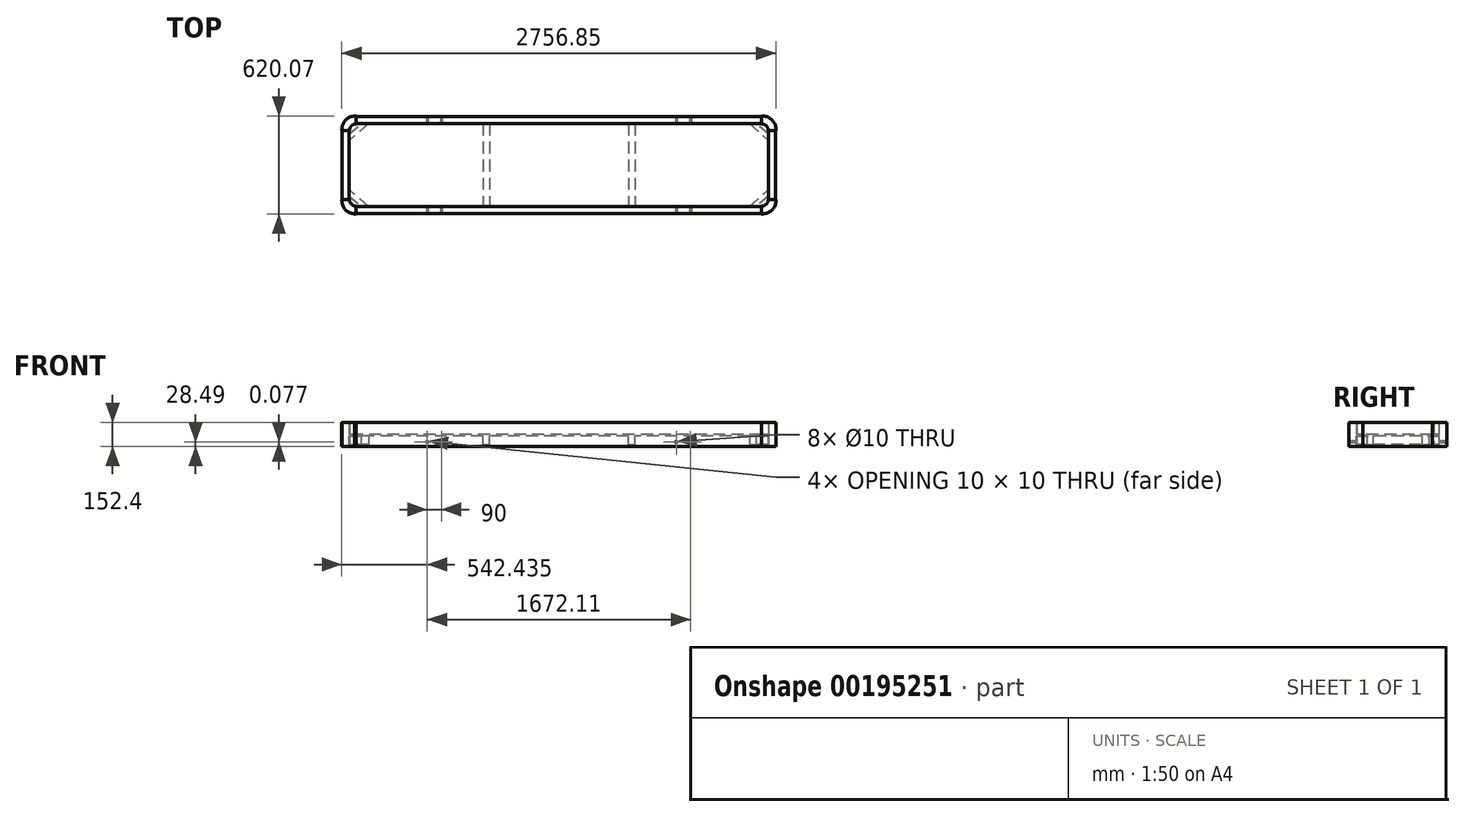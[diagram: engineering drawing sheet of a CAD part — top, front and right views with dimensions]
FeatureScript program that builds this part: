
annotation { "Feature Type Name" : "Feature", "Feature Type Description" : "" }
export const myFeature = defineFeature(function(context is Context, id is Id, definition is map)
    precondition{}
    {
        {
            var Q0;
            Q0=qCreatedBy(makeId("Top.planeOp"),FACE);
            var sketch = newSketch(context, id + "F0", { "sketchPlane" : qUnion([Q0])});
            skLineSegment(sketch, "E0.bottom", {"start": v(-1376.36, -307.98) * mm, "end": v(1376.36, -307.98) * mm});
            skLineSegment(sketch, "E0.top", {"start": v(-1376.36, 307.98) * mm, "end": v(1376.36, 307.98) * mm});
            skLineSegment(sketch, "E0.left", {"start": v(-1376.36, -307.98) * mm, "end": v(-1376.36, 307.98) * mm});
            skLineSegment(sketch, "E0.right", {"start": v(1376.36, -307.98) * mm, "end": v(1376.36, 307.98) * mm});
            skPoint(sketch, "E0.middle", {"position": v(0, 0) * mm});
            skSolve(sketch);
        }
        {
            var Q0;
            Q0=makeQuery(id+"F0.imprint","IMPRINT",FACE,{"disambiguationData":[TD([[makeQuery(id+"F0.imprint","IMPRINT",EDGE,{"derivedFrom":sQuery(id+"F0.wireOp",EDGE,"E0.bottom")}),1.0]])]});
            var Q1;
            Q1 = qSketchRegion(id + "F3", true);
            extrude(context, id + "F1", {"entities" : qUnion([Q0, Q1]), "oppositeDirection" : true, "depth" : 10.16 * mm});
        }
        {
            var Q0;
            Q0=makeQuery(id+"F1.opExtrude","SWEPT_EDGE",EDGE,{"disambiguationData":[OSD([sQuery(id+"F0.wireOp",EDGE,"E0.top"),sQuery(id+"F0.wireOp",EDGE,"E0.right")])]});
            var Q1;
            Q1=makeQuery(id+"F1.opExtrude","SWEPT_EDGE",EDGE,{"disambiguationData":[OSD([sQuery(id+"F0.wireOp",EDGE,"E0.bottom"),sQuery(id+"F0.wireOp",EDGE,"E0.right")])]});
            var Q2;
            Q2=makeQuery(id+"F1.opExtrude","SWEPT_EDGE",EDGE,{"disambiguationData":[OSD([sQuery(id+"F0.wireOp",EDGE,"E0.bottom"),sQuery(id+"F0.wireOp",EDGE,"E0.left")])]});
            var Q3;
            Q3=makeQuery(id+"F1.opExtrude","SWEPT_EDGE",EDGE,{"disambiguationData":[OSD([sQuery(id+"F0.wireOp",EDGE,"E0.top"),sQuery(id+"F0.wireOp",EDGE,"E0.left")])]});
            fillet(context, id + "F2", {"entities" : qUnion([Q0, Q1, Q2, Q3]), "radius" : 80 * mm, "allowEdgeOverflow" : false});
        }
        {
            var Q0;
            Q0=qCreatedBy(makeId("Top.planeOp"),FACE);
            var sketch = newSketch(context, id + "F3", { "sketchPlane" : qUnion([Q0])});
            skArc(sketch, "E1.0", {"start": v(-1296.36, 307.98) * mm, "mid": v(-1352.93, 284.54) * mm, "end": v(-1376.36, 227.98) * mm});
            skLineSegment(sketch, "E1.1", {"start": v(-1376.36, -227.98) * mm, "end": v(-1376.36, 227.98) * mm});
            skLineSegment(sketch, "E1.2", {"start": v(-1296.36, 307.98) * mm, "end": v(1296.36, 307.98) * mm});
            skArc(sketch, "E1.3", {"start": v(-1376.36, -227.98) * mm, "mid": v(-1352.93, -284.54) * mm, "end": v(-1296.36, -307.98) * mm});
            skArc(sketch, "E1.4", {"start": v(1376.36, 227.98) * mm, "mid": v(1352.93, 284.54) * mm, "end": v(1296.36, 307.98) * mm});
            skLineSegment(sketch, "E1.5", {"start": v(1376.36, -227.98) * mm, "end": v(1376.36, 227.98) * mm});
            skArc(sketch, "E1.6", {"start": v(1296.36, -307.98) * mm, "mid": v(1352.93, -284.54) * mm, "end": v(1376.36, -227.98) * mm});
            skLineSegment(sketch, "E1.7", {"start": v(-1296.36, -307.98) * mm, "end": v(1296.36, -307.98) * mm});
            skArc(sketch, "E2.0", {"start": v(-1331.91, -262.98) * mm, "mid": v(-1331.75, -263.36) * mm, "end": v(-1331.36, -263.53) * mm});
            skArc(sketch, "E2.3", {"start": v(-1331.36, 263.53) * mm, "mid": v(-1331.75, 263.36) * mm, "end": v(-1331.91, 262.98) * mm});
            skArc(sketch, "E2.4", {"start": v(1331.36, -263.53) * mm, "mid": v(1331.75, -263.36) * mm, "end": v(1331.91, -262.98) * mm});
            skArc(sketch, "E2.6", {"start": v(1331.91, 262.98) * mm, "mid": v(1331.75, 263.36) * mm, "end": v(1331.36, 263.53) * mm});
            skArc(sketch, "E3.0", {"start": v(-1286.91, 263.53) * mm, "mid": v(-1318.73, 250.34) * mm, "end": v(-1331.91, 218.53) * mm});
            skLineSegment(sketch, "E3.2", {"start": v(-1286.91, 263.53) * mm, "end": v(1286.91, 263.53) * mm});
            skArc(sketch, "E3.4", {"start": v(1331.91, 220.25) * mm, "mid": v(1318.13, 250.95) * mm, "end": v(1286.91, 263.53) * mm});
            skArc(sketch, "E4.MirrorCS", {"start": v(-1286.91, -263.53) * mm, "mid": v(-1318.73, -250.34) * mm, "end": v(-1331.91, -218.53) * mm});
            skLineSegment(sketch, "E5.MirrorCS", {"start": v(-1286.91, -263.53) * mm, "end": v(1286.91, -263.53) * mm});
            skArc(sketch, "E6.MirrorCS", {"start": v(1331.91, -220.25) * mm, "mid": v(1318.13, -250.95) * mm, "end": v(1286.91, -263.53) * mm});
            skLineSegment(sketch, "E7", {"start": v(-1331.91, -218.53) * mm, "end": v(-1331.91, 218.53) * mm});
            skLineSegment(sketch, "E8", {"start": v(1331.91, -220.25) * mm, "end": v(1331.91, 220.25) * mm});
            skSolve(sketch);
        }
        {
            var Q0;
            Q0 = qSketchRegion(id + "F3", true);
            extrude(context, id + "F4", {"entities" : qUnion([Q0]), "operationType" : NewBodyOperationType.ADD, "endBound" : BoundingType.SYMMETRIC, "depth" : 149.86 * mm});
        }
        {
            var Q0;
            Q0=qCreatedBy(makeId("Top.planeOp"),FACE);
            var sketch = newSketch(context, id + "F5", { "sketchPlane" : qUnion([Q0])});
            skArc(sketch, "E9.0", {"start": v(-1378.36, -227.98) * mm, "mid": v(-1354.35, -285.96) * mm, "end": v(-1296.36, -309.98) * mm});
            skArc(sketch, "E10.0", {"start": v(-1296.36, 309.98) * mm, "mid": v(-1354.35, 285.96) * mm, "end": v(-1378.36, 227.98) * mm});
            skArc(sketch, "E11.0", {"start": v(1296.36, -309.98) * mm, "mid": v(1354.35, -285.96) * mm, "end": v(1378.36, -227.98) * mm});
            skArc(sketch, "E12.0", {"start": v(1378.36, 227.98) * mm, "mid": v(1354.35, 285.96) * mm, "end": v(1296.36, 309.98) * mm});
            skArc(sketch, "E13.0", {"start": v(1329.93, 219.82) * mm, "mid": v(1316.4, 249.84) * mm, "end": v(1285.61, 261.5) * mm});
            skArc(sketch, "E14.0", {"start": v(1329.9, -220.42) * mm, "mid": v(1316.53, -249.71) * mm, "end": v(1286.57, -261.52) * mm});
            skArc(sketch, "E15.0", {"start": v(-1286.91, -261.53) * mm, "mid": v(-1317.32, -248.93) * mm, "end": v(-1329.91, -218.53) * mm});
            skArc(sketch, "E16.0", {"start": v(-1286.9, 261.52) * mm, "mid": v(-1317.32, 248.93) * mm, "end": v(-1329.91, 218.53) * mm});
            skLineSegment(sketch, "E17", {"start": v(-1286.9, 261.52) * mm, "end": v(-1286.9, 309.98) * mm});
            skLineSegment(sketch, "E18", {"start": v(-1286.9, 309.98) * mm, "end": v(-1296.36, 309.98) * mm});
            skLineSegment(sketch, "E19", {"start": v(-1329.91, 218.53) * mm, "end": v(-1378.49, 218.53) * mm});
            skLineSegment(sketch, "E20", {"start": v(-1378.49, 218.53) * mm, "end": v(-1378.36, 227.98) * mm});
            skLineSegment(sketch, "E21", {"start": v(1285.61, 261.5) * mm, "end": v(1285.61, 309.98) * mm});
            skLineSegment(sketch, "E22", {"start": v(1285.61, 309.98) * mm, "end": v(1296.36, 309.98) * mm});
            skLineSegment(sketch, "E23", {"start": v(1329.93, 219.82) * mm, "end": v(1378.36, 219.82) * mm});
            skLineSegment(sketch, "E24", {"start": v(1378.36, 219.82) * mm, "end": v(1378.36, 227.98) * mm});
            skLineSegment(sketch, "E25", {"start": v(1286.57, -261.52) * mm, "end": v(1286.57, -309.98) * mm});
            skLineSegment(sketch, "E26", {"start": v(1286.57, -309.98) * mm, "end": v(1296.36, -309.98) * mm});
            skLineSegment(sketch, "E27", {"start": v(1329.9, -220.42) * mm, "end": v(1378.36, -220.42) * mm});
            skLineSegment(sketch, "E28", {"start": v(1378.36, -220.42) * mm, "end": v(1378.36, -227.98) * mm});
            skLineSegment(sketch, "E29", {"start": v(-1329.91, -218.53) * mm, "end": v(-1378.45, -218.53) * mm});
            skLineSegment(sketch, "E30", {"start": v(-1378.45, -218.53) * mm, "end": v(-1378.36, -227.98) * mm});
            skLineSegment(sketch, "E31", {"start": v(-1286.91, -261.53) * mm, "end": v(-1286.91, -310.09) * mm});
            skLineSegment(sketch, "E32", {"start": v(-1286.91, -310.09) * mm, "end": v(-1296.36, -309.98) * mm});
            skSolve(sketch);
        }
        {
            var Q0;
            Q0 = qSketchRegion(id + "F5", true);
            extrude(context, id + "F6", {"entities" : qUnion([Q0]), "operationType" : NewBodyOperationType.ADD, "endBound" : BoundingType.SYMMETRIC, "depth" : 152.4 * mm});
        }
        {
            var Q0;
            Q0=makeQuery(id+"F4.opExtrude","CAP_EDGE",EDGE,{"disambiguationData":[OSD([sQuery(id+"F3.wireOp",EDGE,"E2.5")])],"isStart":false});
            var Q1;
            Q1=makeQuery(id+"F4.opExtrude","CAP_EDGE",EDGE,{"disambiguationData":[OSD([sQuery(id+"F3.wireOp",EDGE,"E1.5")])],"isStart":false});
            var Q2;
            Q2=makeQuery(id+"F4.opExtrude","CAP_EDGE",EDGE,{"disambiguationData":[OSD([sQuery(id+"F3.wireOp",EDGE,"E1.1")])],"isStart":false});
            var Q3;
            Q3=makeQuery(id+"F4.opExtrude","CAP_EDGE",EDGE,{"disambiguationData":[OSD([sQuery(id+"F3.wireOp",EDGE,"E2.1")])],"isStart":false});
            var Q4;
            Q4=makeQuery(id+"F4.opExtrude","CAP_EDGE",EDGE,{"disambiguationData":[OSD([sQuery(id+"F3.wireOp",EDGE,"E2.2")])],"isStart":false});
            var Q5;
            Q5=makeQuery(id+"F4.opExtrude","CAP_EDGE",EDGE,{"disambiguationData":[OSD([sQuery(id+"F3.wireOp",EDGE,"E1.7")])],"isStart":false});
            var Q6;
            Q6=makeQuery(id+"F4.opExtrude","CAP_EDGE",EDGE,{"disambiguationData":[OSD([sQuery(id+"F3.wireOp",EDGE,"E1.2")])],"isStart":false});
            var Q7;
            Q7=makeQuery(id+"F4.opExtrude","CAP_EDGE",EDGE,{"disambiguationData":[OSD([sQuery(id+"F3.wireOp",EDGE,"E2.7")])],"isStart":false});
            fillet(context, id + "F7", {"entities" : qUnion([Q0, Q1, Q2, Q3, Q4, Q5, Q6, Q7]), "radius" : .4 * mm, "tangentPropagation" : true, "allowEdgeOverflow" : false});
        }
        {
            var Q0;
            Q0=makeQuery(id+"F6.opExtrude","CAP_EDGE",EDGE,{"disambiguationData":[OSD([sQuery(id+"F5.wireOp",EDGE,"E9.0")])],"isStart":true});
            var Q1;
            Q1=makeQuery(id+"F6.opExtrude","CAP_EDGE",EDGE,{"disambiguationData":[OSD([sQuery(id+"F5.wireOp",EDGE,"E30")])],"isStart":true});
            var Q2;
            Q2=makeQuery(id+"F6.opExtrude","CAP_EDGE",EDGE,{"disambiguationData":[OSD([sQuery(id+"F5.wireOp",EDGE,"E32")])],"isStart":true});
            var Q3;
            Q3=makeQuery(id+"F6.opExtrude","CAP_EDGE",EDGE,{"disambiguationData":[OSD([sQuery(id+"F5.wireOp",EDGE,"E15.0")])],"isStart":true});
            var Q4;
            Q4=makeQuery(id+"F6.opExtrude","CAP_EDGE",EDGE,{"disambiguationData":[OSD([sQuery(id+"F5.wireOp",EDGE,"E20")])],"isStart":true});
            var Q5;
            Q5=makeQuery(id+"F6.opExtrude","CAP_EDGE",EDGE,{"disambiguationData":[OSD([sQuery(id+"F5.wireOp",EDGE,"E10.0")])],"isStart":true});
            var Q6;
            Q6=makeQuery(id+"F6.opExtrude","CAP_EDGE",EDGE,{"disambiguationData":[OSD([sQuery(id+"F5.wireOp",EDGE,"E18")])],"isStart":true});
            var Q7;
            Q7=makeQuery(id+"F6.opExtrude","CAP_EDGE",EDGE,{"disambiguationData":[OSD([sQuery(id+"F5.wireOp",EDGE,"E16.0")])],"isStart":true});
            var Q8;
            Q8=makeQuery(id+"F6.opExtrude","CAP_EDGE",EDGE,{"disambiguationData":[OSD([sQuery(id+"F5.wireOp",EDGE,"E11.0")])],"isStart":true});
            var Q9;
            Q9=makeQuery(id+"F6.opExtrude","CAP_EDGE",EDGE,{"disambiguationData":[OSD([sQuery(id+"F5.wireOp",EDGE,"E14.0")])],"isStart":true});
            var Q10;
            Q10=makeQuery(id+"F6.opExtrude","CAP_EDGE",EDGE,{"disambiguationData":[OSD([sQuery(id+"F5.wireOp",EDGE,"E26")])],"isStart":true});
            var Q11;
            Q11=makeQuery(id+"F6.opExtrude","CAP_EDGE",EDGE,{"disambiguationData":[OSD([sQuery(id+"F5.wireOp",EDGE,"E28")])],"isStart":true});
            var Q12;
            Q12=makeQuery(id+"F6.opExtrude","CAP_EDGE",EDGE,{"disambiguationData":[OSD([sQuery(id+"F5.wireOp",EDGE,"E13.0")])],"isStart":true});
            var Q13;
            Q13=makeQuery(id+"F6.opExtrude","CAP_EDGE",EDGE,{"disambiguationData":[OSD([sQuery(id+"F5.wireOp",EDGE,"E24")])],"isStart":true});
            var Q14;
            Q14=makeQuery(id+"F6.opExtrude","CAP_EDGE",EDGE,{"disambiguationData":[OSD([sQuery(id+"F5.wireOp",EDGE,"E22")])],"isStart":true});
            var Q15;
            Q15=makeQuery(id+"F6.opExtrude","CAP_EDGE",EDGE,{"disambiguationData":[OSD([sQuery(id+"F5.wireOp",EDGE,"E12.0")])],"isStart":true});
            var Q16;
            Q16=makeQuery(id+"F6.opExtrude","SWEPT_EDGE",EDGE,{"disambiguationData":[OSD([sQuery(id+"F5.wireOp",EDGE,"E25"),sQuery(id+"F5.wireOp",EDGE,"E26")])]});
            var Q17;
            Q17=makeQuery(id+"F6.opExtrude","CAP_EDGE",EDGE,{"disambiguationData":[OSD([sQuery(id+"F5.wireOp",EDGE,"E15.0")])],"isStart":false});
            var Q18;
            Q18=makeQuery(id+"F6.opExtrude","CAP_EDGE",EDGE,{"disambiguationData":[OSD([sQuery(id+"F5.wireOp",EDGE,"E30")])],"isStart":false});
            var Q19;
            Q19=makeQuery(id+"F6.opExtrude","CAP_EDGE",EDGE,{"disambiguationData":[OSD([sQuery(id+"F5.wireOp",EDGE,"E9.0")])],"isStart":false});
            var Q20;
            Q20=makeQuery(id+"F6.opExtrude","CAP_EDGE",EDGE,{"disambiguationData":[OSD([sQuery(id+"F5.wireOp",EDGE,"E32")])],"isStart":false});
            var Q21;
            Q21=makeQuery(id+"F6.opExtrude","CAP_EDGE",EDGE,{"disambiguationData":[OSD([sQuery(id+"F5.wireOp",EDGE,"E16.0")])],"isStart":false});
            var Q22;
            Q22=makeQuery(id+"F6.opExtrude","CAP_EDGE",EDGE,{"disambiguationData":[OSD([sQuery(id+"F5.wireOp",EDGE,"E18")])],"isStart":false});
            var Q23;
            Q23=makeQuery(id+"F6.opExtrude","CAP_EDGE",EDGE,{"disambiguationData":[OSD([sQuery(id+"F5.wireOp",EDGE,"E10.0")])],"isStart":false});
            var Q24;
            Q24=makeQuery(id+"F6.opExtrude","CAP_EDGE",EDGE,{"disambiguationData":[OSD([sQuery(id+"F5.wireOp",EDGE,"E20")])],"isStart":false});
            var Q25;
            Q25=makeQuery(id+"F6.opExtrude","CAP_EDGE",EDGE,{"disambiguationData":[OSD([sQuery(id+"F5.wireOp",EDGE,"E14.0")])],"isStart":false});
            var Q26;
            Q26=makeQuery(id+"F6.opExtrude","CAP_EDGE",EDGE,{"disambiguationData":[OSD([sQuery(id+"F5.wireOp",EDGE,"E28")])],"isStart":false});
            var Q27;
            Q27=makeQuery(id+"F6.opExtrude","CAP_EDGE",EDGE,{"disambiguationData":[OSD([sQuery(id+"F5.wireOp",EDGE,"E11.0")])],"isStart":false});
            var Q28;
            Q28=makeQuery(id+"F6.opExtrude","CAP_EDGE",EDGE,{"disambiguationData":[OSD([sQuery(id+"F5.wireOp",EDGE,"E26")])],"isStart":false});
            var Q29;
            Q29=makeQuery(id+"F6.opExtrude","CAP_EDGE",EDGE,{"disambiguationData":[OSD([sQuery(id+"F5.wireOp",EDGE,"E12.0")])],"isStart":false});
            var Q30;
            Q30=makeQuery(id+"F6.opExtrude","CAP_EDGE",EDGE,{"disambiguationData":[OSD([sQuery(id+"F5.wireOp",EDGE,"E22")])],"isStart":false});
            var Q31;
            Q31=makeQuery(id+"F6.opExtrude","CAP_EDGE",EDGE,{"disambiguationData":[OSD([sQuery(id+"F5.wireOp",EDGE,"E13.0")])],"isStart":false});
            var Q32;
            Q32=makeQuery(id+"F6.opExtrude","CAP_EDGE",EDGE,{"disambiguationData":[OSD([sQuery(id+"F5.wireOp",EDGE,"E24")])],"isStart":false});
            fillet(context, id + "F8", {"entities" : qUnion([Q0, Q1, Q2, Q3, Q4, Q5, Q6, Q7, Q8, Q9, Q10, Q11, Q12, Q13, Q14, Q15, Q16, Q17, Q18, Q19, Q20, Q21, Q22, Q23, Q24, Q25, Q26, Q27, Q28, Q29, Q30, Q31, Q32]), "radius" : 1 * mm, "tangentPropagation" : true, "allowEdgeOverflow" : false});
        }
        {
            var Q0;
            Q0=qCreatedBy(makeId("Top.planeOp"),FACE);
            var sketch = newSketch(context, id + "F9", { "sketchPlane" : qUnion([Q0])});
            skLineSegment(sketch, "E33.bottom", {"start": v(-1359.8, 171.57) * mm, "end": v(-1220.1, 171.57) * mm, "construction": true});
            skLineSegment(sketch, "E33.left", {"start": v(-1330.9, 167.86) * mm, "end": v(-1330.9, 307.56) * mm, "construction": true});
            skLineSegment(sketch, "E34", {"start": v(-1359.8, 171.57) * mm, "end": v(-1233.38, 281.66) * mm});
            skLineSegment(sketch, "E35", {"start": v(-1189.58, 281.66) * mm, "end": v(-1233.38, 281.66) * mm});
            skLineSegment(sketch, "E36", {"start": v(-1189.58, 281.66) * mm, "end": v(-1342.65, 147.07) * mm});
            skLineSegment(sketch, "E37", {"start": v(-1359.8, 171.57) * mm, "end": v(-1342.65, 147.07) * mm});
            skLineSegment(sketch, "E38.MirrorCS", {"start": v(1359.8, 171.57) * mm, "end": v(1342.65, 147.07) * mm});
            skLineSegment(sketch, "E39.MirrorCS", {"start": v(1359.8, 171.57) * mm, "end": v(1233.38, 281.66) * mm});
            skLineSegment(sketch, "E40.MirrorCS", {"start": v(1189.58, 281.66) * mm, "end": v(1233.38, 281.66) * mm});
            skLineSegment(sketch, "E41.MirrorCS", {"start": v(1359.8, 171.57) * mm, "end": v(1220.1, 171.57) * mm, "construction": true});
            skLineSegment(sketch, "E42.MirrorCS", {"start": v(1330.9, 167.86) * mm, "end": v(1330.9, 307.56) * mm, "construction": true});
            skLineSegment(sketch, "E43.MirrorCS", {"start": v(1189.58, 281.66) * mm, "end": v(1342.65, 147.07) * mm});
            skLineSegment(sketch, "E44.MirrorCS", {"start": v(1359.8, -171.57) * mm, "end": v(1342.65, -147.07) * mm});
            skLineSegment(sketch, "E45.MirrorCS", {"start": v(-1359.8, -171.57) * mm, "end": v(-1342.65, -147.07) * mm});
            skLineSegment(sketch, "E46.MirrorCS", {"start": v(1189.58, -281.66) * mm, "end": v(1233.38, -281.66) * mm});
            skLineSegment(sketch, "E47.MirrorCS", {"start": v(-1359.8, -171.57) * mm, "end": v(-1233.38, -281.66) * mm});
            skLineSegment(sketch, "E48.MirrorCS", {"start": v(-1330.9, -167.86) * mm, "end": v(-1330.9, -307.56) * mm, "construction": true});
            skLineSegment(sketch, "E49.MirrorCS", {"start": v(-1189.58, -281.66) * mm, "end": v(-1233.38, -281.66) * mm});
            skLineSegment(sketch, "E50.MirrorCS", {"start": v(-1359.8, -171.57) * mm, "end": v(-1220.1, -171.57) * mm, "construction": true});
            skLineSegment(sketch, "E51.MirrorCS", {"start": v(-1189.58, -281.66) * mm, "end": v(-1342.65, -147.07) * mm});
            skLineSegment(sketch, "E52.MirrorCS", {"start": v(1189.58, -281.66) * mm, "end": v(1342.65, -147.07) * mm});
            skLineSegment(sketch, "E53.MirrorCS", {"start": v(1359.8, -171.57) * mm, "end": v(1233.38, -281.66) * mm});
            skLineSegment(sketch, "E54.MirrorCS", {"start": v(1330.9, -167.86) * mm, "end": v(1330.9, -307.56) * mm, "construction": true});
            skLineSegment(sketch, "E55.MirrorCS", {"start": v(1359.8, -171.57) * mm, "end": v(1220.1, -171.57) * mm, "construction": true});
            skLineSegment(sketch, "E56", {"start": v(461.96, 299.9) * mm, "end": v(461.96, -14.21) * mm, "construction": true});
            skLineSegment(sketch, "E57.bottom", {"start": v(482.28, 299.9) * mm, "end": v(441.64, 299.9) * mm});
            skLineSegment(sketch, "E57.top", {"start": v(482.28, -300.1) * mm, "end": v(441.64, -300.1) * mm});
            skLineSegment(sketch, "E57.left", {"start": v(482.28, 299.9) * mm, "end": v(482.28, -300.1) * mm});
            skLineSegment(sketch, "E57.right", {"start": v(441.64, 299.9) * mm, "end": v(441.64, -300.1) * mm});
            skPoint(sketch, "E57.middle", {"position": v(461.96, -0.1) * mm});
            skLineSegment(sketch, "E58.MirrorCS", {"start": v(441.64, -300.1) * mm, "end": v(482.28, -300.1) * mm});
            skLineSegment(sketch, "E59.MirrorCS", {"start": v(441.64, 299.9) * mm, "end": v(482.28, 299.9) * mm});
            skLineSegment(sketch, "E60.MirrorCS", {"start": v(-482.28, 299.9) * mm, "end": v(-441.64, 299.9) * mm});
            skPoint(sketch, "E61.MirrorP", {"position": v(-461.96, -0.1) * mm});
            skLineSegment(sketch, "E62.MirrorCS", {"start": v(-482.28, 299.9) * mm, "end": v(-482.28, -300.1) * mm});
            skLineSegment(sketch, "E63.MirrorCS", {"start": v(-441.64, 299.9) * mm, "end": v(-441.64, -300.1) * mm});
            skLineSegment(sketch, "E64.MirrorCS", {"start": v(-441.64, -300.1) * mm, "end": v(-482.28, -300.1) * mm});
            skLineSegment(sketch, "E65.MirrorCS", {"start": v(-441.64, 299.9) * mm, "end": v(-482.28, 299.9) * mm});
            skLineSegment(sketch, "E66.MirrorCS", {"start": v(-461.96, 299.9) * mm, "end": v(-461.96, -14.21) * mm, "construction": true});
            skLineSegment(sketch, "E67.MirrorCS", {"start": v(-482.28, -300.1) * mm, "end": v(-441.64, -300.1) * mm});
            skSolve(sketch);
        }
        {
            var Q0;
            Q0 = qSketchRegion(id + "F9", true);
            extrude(context, id + "F10", {"entities" : qUnion([Q0]), "operationType" : NewBodyOperationType.ADD, "oppositeDirection" : true, "depth" : 63 * mm});
        }
        {
            var Q0;
            Q0=qCreatedBy(makeId("Front.planeOp"),FACE);
            var sketch = newSketch(context, id + "F11", { "sketchPlane" : qUnion([Q0])});
            skLineSegment(sketch, "E68", {"start": v(-1378.45, 0) * mm, "end": v(-845.05, 0) * mm, "construction": true});
            skLineSegment(sketch, "E69", {"start": v(-845.05, 0) * mm, "end": v(-845.05, -74.71) * mm, "construction": true});
            skLineSegment(sketch, "E70", {"start": v(-845.05, -74.71) * mm, "end": v(-836.05, -74.71) * mm, "construction": true});
            skLineSegment(sketch, "E71", {"start": v(-836.05, -74.71) * mm, "end": v(-836.05, -56.71) * mm, "construction": true});
            skLineSegment(sketch, "E72", {"start": v(-836.05, -56.71) * mm, "end": v(-836.05, -47.71) * mm, "construction": true});
            skCircle(sketch, "E73", {"center": v(-836.05, -47.71) * mm, "radius": 9 * mm, "construction": true});
            skLineSegment(sketch, "E74", {"start": v(-827.05, -47.63) * mm, "end": v(-755.05, -47.63) * mm, "construction": true});
            skLineSegment(sketch, "E75", {"start": v(-755.05, -47.63) * mm, "end": v(-746.05, -47.63) * mm, "construction": true});
            skCircle(sketch, "E76", {"center": v(-746.05, -47.63) * mm, "radius": 9 * mm, "construction": true});
            skCircle(sketch, "E77", {"center": v(-836.05, -47.71) * mm, "radius": 5 * mm});
            skCircle(sketch, "E78", {"center": v(-746.05, -47.63) * mm, "radius": 5 * mm});
            skLineSegment(sketch, "E79.0", {"start": v(-1378.45, 75.2) * mm, "end": v(-1378.45, -75.2) * mm, "construction": true});
            skCircle(sketch, "E80.MirrorC", {"center": v(836.05, -47.71) * mm, "radius": 5 * mm});
            skLineSegment(sketch, "E81.MirrorCS", {"start": v(755.05, -47.63) * mm, "end": v(746.05, -47.63) * mm, "construction": true});
            skCircle(sketch, "E82.MirrorC", {"center": v(746.05, -47.63) * mm, "radius": 5 * mm});
            skLineSegment(sketch, "E83.MirrorCS", {"start": v(836.05, -56.71) * mm, "end": v(836.05, -47.71) * mm, "construction": true});
            skCircle(sketch, "E84.MirrorC", {"center": v(836.05, -47.71) * mm, "radius": 9 * mm, "construction": true});
            skLineSegment(sketch, "E85.MirrorCS", {"start": v(827.05, -47.63) * mm, "end": v(755.05, -47.63) * mm, "construction": true});
            skLineSegment(sketch, "E86.MirrorCS", {"start": v(845.05, -74.71) * mm, "end": v(836.05, -74.71) * mm, "construction": true});
            skCircle(sketch, "E87.MirrorC", {"center": v(746.05, -47.63) * mm, "radius": 9 * mm, "construction": true});
            skLineSegment(sketch, "E88.MirrorCS", {"start": v(845.05, 0) * mm, "end": v(845.05, -74.71) * mm, "construction": true});
            skLineSegment(sketch, "E89.MirrorCS", {"start": v(836.05, -74.71) * mm, "end": v(836.05, -56.71) * mm, "construction": true});
            skLineSegment(sketch, "E90.MirrorCS", {"start": v(1378.45, 0) * mm, "end": v(845.05, 0) * mm, "construction": true});
            skLineSegment(sketch, "E91.MirrorCS", {"start": v(1378.45, 75.2) * mm, "end": v(1378.45, -75.2) * mm, "construction": true});
            skLineSegment(sketch, "E92", {"start": v(-1378.45, 75.2) * mm, "end": v(0, 75.2) * mm, "construction": true});
            skSolve(sketch);
        }
        {
            var Q0;
            Q0 = qSketchRegion(id + "F11", true);
            var Q1;
            {var subQ1=sQuery(id+"F3.wireOp",EDGE,"E1.7");Q1=makeQuery(id+"F4.boolean.opBoolean","SPLIT",FACE,{"disambiguationData":[TD([makeQuery(id+"F1.opExtrude","CAP_FACE",FACE,{"disambiguationData":[OSD([sQuery(id+"F0.wireOp",EDGE,"E0.bottom"),sQuery(id+"F0.wireOp",EDGE,"E0.top"),sQuery(id+"F0.wireOp",EDGE,"E0.left"),sQuery(id+"F0.wireOp",EDGE,"E0.right")])],"isStart":false})])],"derivedFrom":makeQuery(id+"F4.opExtrude","SWEPT_FACE",FACE,{"disambiguationData":[OSD([subQ1])]})});}
            extrude(context, id + "F12", {"entities" : qUnion([Q0]), "operationType" : NewBodyOperationType.REMOVE, "endBound" : BoundingType.THROUGH_ALL, "oppositeDirection" : true, "endBoundEntityFace" : qUnion([Q1]), "depth" : 25 * mm, "hasSecondDirection" : true, "secondDirectionOppositeDirection" : false, "secondDirectionDepth" : 512 * mm});
        }
    });
